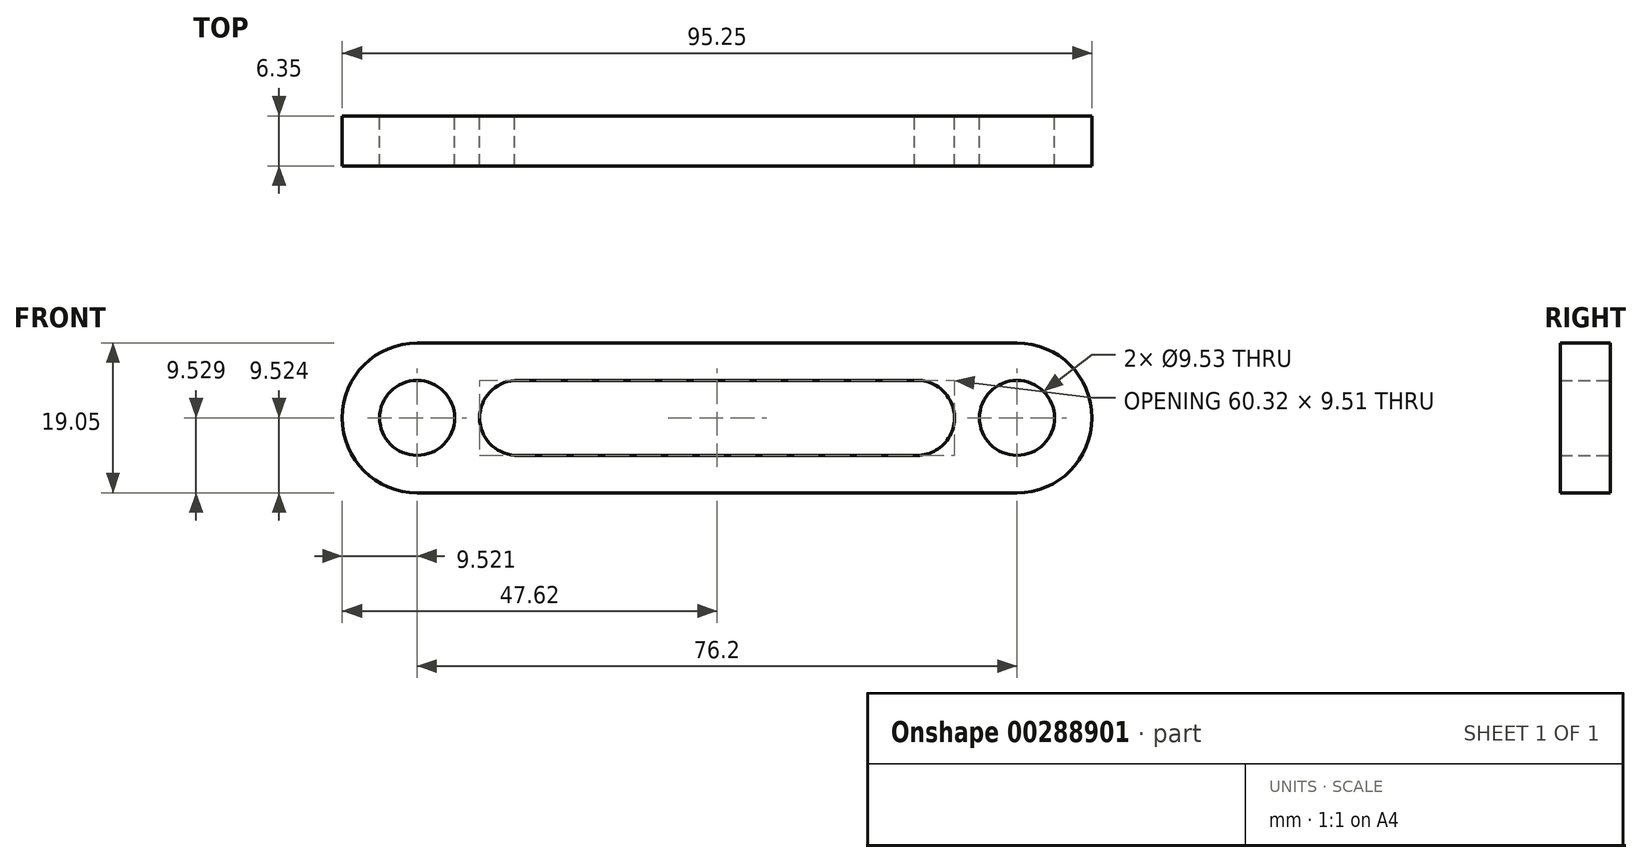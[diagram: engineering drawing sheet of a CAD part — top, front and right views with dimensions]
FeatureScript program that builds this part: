
annotation { "Feature Type Name" : "Feature", "Feature Type Description" : "" }
export const myFeature = defineFeature(function(context is Context, id is Id, definition is map)
    precondition{}
    {
        {
            var Q0;
            Q0=qCreatedBy(makeId("Front.planeOp"),FACE);
            var sketch = newSketch(context, id + "F0", { "sketchPlane" : qUnion([Q0])});
            skLineSegment(sketch, "E0.bottom", {"start": v(-28.46, 22.44) * mm, "end": v(47.74, 22.44) * mm});
            skLineSegment(sketch, "E0.top", {"start": v(-28.46, 3.4) * mm, "end": v(47.74, 3.4) * mm});
            skLineSegment(sketch, "E0.left", {"start": v(-28.46, 22.44) * mm, "end": v(-28.46, 17.68) * mm});
            skLineSegment(sketch, "E0.right", {"start": v(47.74, 22.44) * mm, "end": v(47.74, 17.68) * mm});
            skArc(sketch, "E1", {"start": v(-28.46, 22.44) * mm, "mid": v(-37.98, 12.92) * mm, "end": v(-28.46, 3.4) * mm});
            skArc(sketch, "E2", {"start": v(47.74, 3.4) * mm, "mid": v(57.27, 12.92) * mm, "end": v(47.74, 22.44) * mm});
            skCircle(sketch, "E3", {"center": v(-28.46, 12.92) * mm, "radius": 4.76 * mm});
            skCircle(sketch, "E4", {"center": v(47.74, 12.92) * mm, "radius": 4.76 * mm});
            skArc(sketch, "E5", {"start": v(35.02, 8.16) * mm, "mid": v(39.8, 13.07) * mm, "end": v(34.72, 17.67) * mm});
            skArc(sketch, "E6", {"start": v(-16.08, 17.67) * mm, "mid": v(-20.52, 12.75) * mm, "end": v(-15.74, 8.16) * mm});
            skLineSegment(sketch, "E7.bottom", {"start": v(-16.08, 17.67) * mm, "end": v(35.06, 17.67) * mm});
            skLineSegment(sketch, "E7.top", {"start": v(-16.08, 8.16) * mm, "end": v(35.06, 8.16) * mm});
            skLineSegment(sketch, "E7.left", {"start": v(-16.08, 8.17) * mm, "end": v(-16.08, 8.16) * mm});
            skLineSegment(sketch, "E8.trimOffspring", {"start": v(-28.46, 8.16) * mm, "end": v(-28.46, 3.4) * mm});
            skSolve(sketch);
        }
        {
            var Q0;
            {var subQ0=sQuery(id+"F0.wireOp",EDGE,"E0.left");Q0=makeQuery(id+"F0.imprint","IMPRINT",FACE,{"disambiguationData":[TD([[makeQuery(id+"F0.imprint","IMPRINT",EDGE,{"derivedFrom":subQ0}),-1.0]])]});}
            var Q1;
            Q1=makeQuery(id+"F0.imprint","IMPRINT",FACE,{"disambiguationData":[TD([[makeQuery(id+"F0.imprint","IMPRINT",EDGE,{"derivedFrom":sQuery(id+"F0.wireOp",EDGE,"E0.bottom")}),-1.0]])]});
            extrude(context, id + "F1", {"entities" : qUnion([Q0, Q1]), "depth" : 6.35 * mm});
        }
    });
